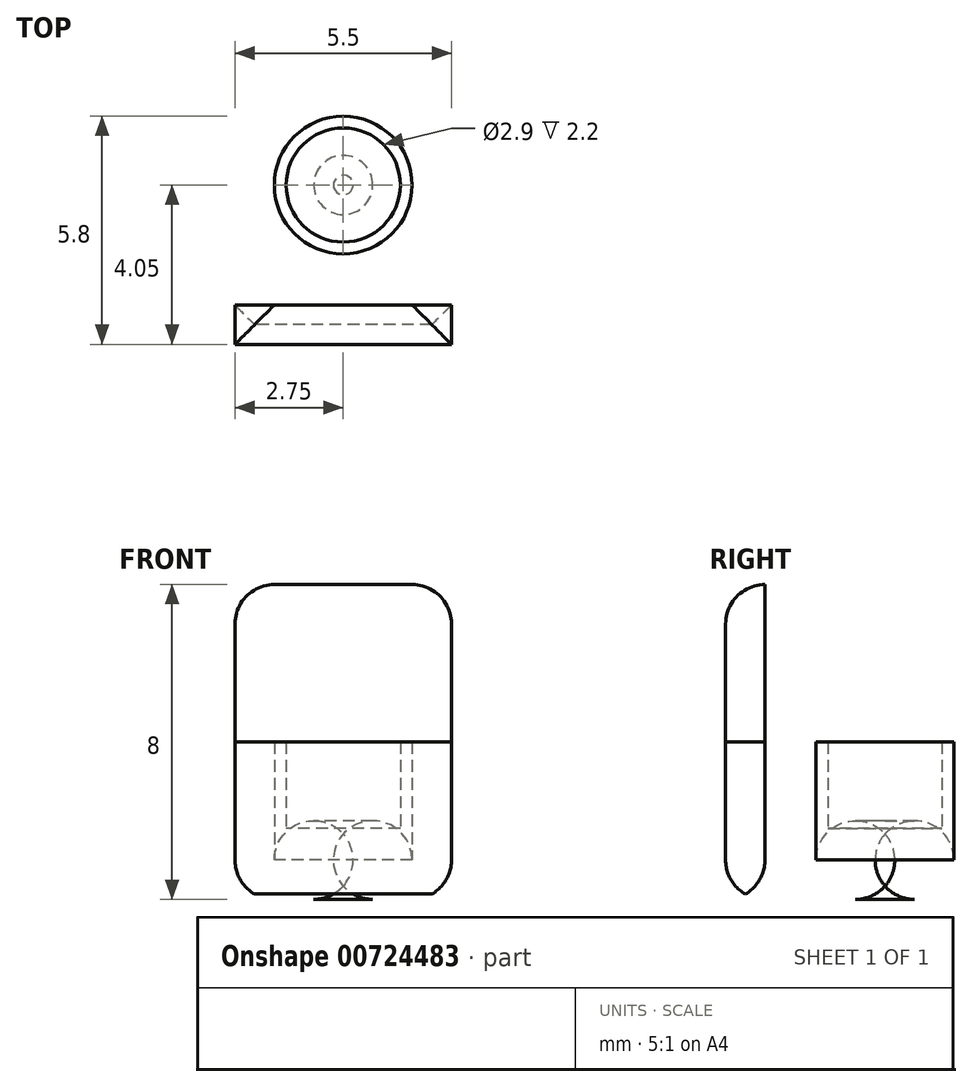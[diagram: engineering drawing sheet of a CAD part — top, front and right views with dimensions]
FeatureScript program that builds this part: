
annotation { "Feature Type Name" : "Feature", "Feature Type Description" : "" }
export const myFeature = defineFeature(function(context is Context, id is Id, definition is map)
    precondition{}
    {
        {
            var Q0;
            Q0=qCreatedBy(makeId("Top.planeOp"),FACE);
            var sketch = newSketch(context, id + "F0", { "sketchPlane" : qUnion([Q0])});
            skCircle(sketch, "E0", {"center": v(0, 4.05) * mm, "radius": 1.45 * mm});
            skLineSegment(sketch, "E1.bottom", {"start": v(0, 0) * mm, "end": v(2.75, 0) * mm});
            skLineSegment(sketch, "E1.top", {"start": v(0, 1) * mm, "end": v(2.75, 1) * mm});
            skLineSegment(sketch, "E1.left", {"start": v(0, 0) * mm, "end": v(0, 1) * mm});
            skLineSegment(sketch, "E1.right", {"start": v(2.75, 0) * mm, "end": v(2.75, 1) * mm});
            skCircle(sketch, "E2", {"center": v(0, 4.05) * mm, "radius": 1.75 * mm});
            skLineSegment(sketch, "E3", {"start": v(2.75, 1) * mm, "end": v(1.68, 4.56) * mm});
            skLineSegment(sketch, "E4", {"start": v(0, 1) * mm, "end": v(0, 2.3) * mm});
            skLineSegment(sketch, "E5.MirrorCS", {"start": v(-2.75, 1) * mm, "end": v(-1.68, 4.56) * mm});
            skLineSegment(sketch, "E6.MirrorCS", {"start": v(-2.75, 0) * mm, "end": v(-2.75, 1) * mm});
            skLineSegment(sketch, "E7.MirrorCS", {"start": v(0, 0) * mm, "end": v(-2.75, 0) * mm});
            skLineSegment(sketch, "E8.MirrorCS", {"start": v(0, 1) * mm, "end": v(-2.75, 1) * mm});
            skSolve(sketch);
        }
        {
            var Q0;
            Q0=makeQuery(id+"F0.imprint","IMPRINT",FACE,{"disambiguationData":[TD([[makeQuery(id+"F0.imprint","IMPRINT",EDGE,{"derivedFrom":sQuery(id+"F0.wireOp",EDGE,"E1.bottom")}),1.0]])]});
            var Q1;
            Q1=makeQuery(id+"F0.imprint","IMPRINT",FACE,{"disambiguationData":[TD([[makeQuery(id+"F0.imprint","IMPRINT",EDGE,{"derivedFrom":sQuery(id+"F0.wireOp",EDGE,"E1.left")}),1.0]])]});
            var Q2;
            Q2=makeQuery(id+"F0.imprint","IMPRINT",FACE,{"disambiguationData":[TD([[makeQuery(id+"F0.imprint","IMPRINT",EDGE,{"derivedFrom":sQuery(id+"F0.wireOp",EDGE,"E1.top")}),1.0]])]});
            var Q3;
            {var subQ0=sQuery(id+"F0.wireOp",EDGE,"E4");Q3=makeQuery(id+"F0.imprint","IMPRINT",FACE,{"disambiguationData":[TD([[makeQuery(id+"F0.imprint","IMPRINT",EDGE,{"derivedFrom":subQ0}),1.0]])]});}
            var Q4;
            Q4=makeQuery(id+"F0.imprint","IMPRINT",FACE,{"disambiguationData":[TD([[makeQuery(id+"F0.imprint","IMPRINT",EDGE,{"derivedFrom":sQuery(id+"F0.wireOp",EDGE,"E0")}),1.0]])]});
            var Q5;
            Q5=makeQuery(id+"F0.imprint","IMPRINT",FACE,{"disambiguationData":[TD([[makeQuery(id+"F0.imprint","IMPRINT",EDGE,{"derivedFrom":sQuery(id+"F0.wireOp",EDGE,"E0")}),-1.0]])]});
            extrude(context, id + "F1", {"entities" : qUnion([Q0, Q1, Q2, Q3, Q4, Q5]), "depth" : 1.8 * mm, "offsetDistance" : 25 * mm});
        }
        {
            var Q0;
            Q0=makeQuery(id+"F0.imprint","IMPRINT",FACE,{"disambiguationData":[TD([[makeQuery(id+"F0.imprint","IMPRINT",EDGE,{"derivedFrom":sQuery(id+"F0.wireOp",EDGE,"E0")}),-1.0]])]});
            var Q1;
            Q1=makeQuery(id+"F0.imprint","IMPRINT",FACE,{"disambiguationData":[TD([[makeQuery(id+"F0.imprint","IMPRINT",EDGE,{"derivedFrom":sQuery(id+"F0.wireOp",EDGE,"E1.left")}),1.0]])]});
            var Q2;
            Q2=makeQuery(id+"F0.imprint","IMPRINT",FACE,{"disambiguationData":[TD([[makeQuery(id+"F0.imprint","IMPRINT",EDGE,{"derivedFrom":sQuery(id+"F0.wireOp",EDGE,"E1.bottom")}),1.0]])]});
            extrude(context, id + "F2", {"entities" : qUnion([Q0, Q1, Q2]), "operationType" : NewBodyOperationType.ADD, "depth" : 4 * mm, "offsetDistance" : 25 * mm});
        }
        {
            var Q0;
            Q0=qCreatedBy(makeId("Top.planeOp"),FACE);
            cPlane(context, id + "F3", {"entities" : qUnion([Q0]), "cplaneType" : CPlaneType.OFFSET, "offset" : 4 * mm, "width" : 150 * mm, "height" : 150 * mm});
        }
        {
            var Q0;
            Q0=makeQuery(id+"F1.opExtrude","SWEPT_BODY",BODY,{"disambiguationData":[OSD([sQuery(id+"F0.wireOp",EDGE,"E1.bottom"),sQuery(id+"F0.wireOp",EDGE,"E1.right"),sQuery(id+"F0.wireOp",EDGE,"E3"),sQuery(id+"F0.wireOp",EDGE,"E2"),sQuery(id+"F0.wireOp",EDGE,"E5.MirrorCS"),sQuery(id+"F0.wireOp",EDGE,"E6.MirrorCS"),sQuery(id+"F0.wireOp",EDGE,"E7.MirrorCS")])]});
            var Q1;
            Q1=qCreatedBy(id+"F3.planeOp",FACE);
            mirror(context, id + "F4", {"operationType" : NewBodyOperationType.ADD, "entities" : qUnion([Q0]), "mirrorPlane" : qUnion([Q1])});
        }
        {
            var Q0;
            Q0=makeQuery(id+"F4.opPattern","COPY",EDGE,{"derivedFrom":makeQuery(id+"F1.opExtrude","CAP_EDGE",EDGE,{"disambiguationData":[OSD([sQuery(id+"F0.wireOp",EDGE,"E3")])],"isStart":true}),"instanceName":"1"});
            var Q1;
            Q1=makeQuery(id+"F4.opPattern","COPY",EDGE,{"derivedFrom":makeQuery(id+"F1.opExtrude","CAP_EDGE",EDGE,{"disambiguationData":[OSD([sQuery(id+"F0.wireOp",EDGE,"E2")])],"isStart":true}),"instanceName":"1"});
            var Q2;
            Q2=makeQuery(id+"F4.opPattern","COPY",EDGE,{"derivedFrom":makeQuery(id+"F1.opExtrude","CAP_EDGE",EDGE,{"disambiguationData":[OSD([sQuery(id+"F0.wireOp",EDGE,"E5.MirrorCS")])],"isStart":true}),"instanceName":"1"});
            var Q3;
            Q3=makeQuery(id+"F4.opPattern","COPY",EDGE,{"derivedFrom":makeQuery(id+"F1.opExtrude","CAP_EDGE",EDGE,{"disambiguationData":[OSD([sQuery(id+"F0.wireOp",EDGE,"E6.MirrorCS")])],"isStart":true}),"instanceName":"1"});
            var Q4;
            Q4=makeQuery(id+"F4.opPattern","COPY",EDGE,{"derivedFrom":makeQuery(id+"F1.opExtrude","CAP_EDGE",EDGE,{"disambiguationData":[OSD([sQuery(id+"F0.wireOp",EDGE,"E1.bottom"),sQuery(id+"F0.wireOp",EDGE,"E7.MirrorCS")])],"isStart":true}),"instanceName":"1"});
            var Q5;
            Q5=makeQuery(id+"F4.opPattern","COPY",EDGE,{"derivedFrom":makeQuery(id+"F1.opExtrude","CAP_EDGE",EDGE,{"disambiguationData":[OSD([sQuery(id+"F0.wireOp",EDGE,"E1.right")])],"isStart":true}),"instanceName":"1"});
            var Q6;
            Q6=makeQuery(id+"F1.opExtrude","CAP_EDGE",EDGE,{"disambiguationData":[OSD([sQuery(id+"F0.wireOp",EDGE,"E3")])],"isStart":true});
            var Q7;
            Q7=makeQuery(id+"F1.opExtrude","CAP_FACE",FACE,{"disambiguationData":[OSD([sQuery(id+"F0.wireOp",EDGE,"E1.bottom"),sQuery(id+"F0.wireOp",EDGE,"E1.right"),sQuery(id+"F0.wireOp",EDGE,"E3"),sQuery(id+"F0.wireOp",EDGE,"E2"),sQuery(id+"F0.wireOp",EDGE,"E5.MirrorCS"),sQuery(id+"F0.wireOp",EDGE,"E6.MirrorCS"),sQuery(id+"F0.wireOp",EDGE,"E7.MirrorCS")])],"isStart":true});
            var Q8;
            Q8=makeQuery(id+"F1.opExtrude","CAP_EDGE",EDGE,{"disambiguationData":[OSD([sQuery(id+"F0.wireOp",EDGE,"E2")])],"isStart":true});
            var Q9;
            Q9=makeQuery(id+"F1.opExtrude","CAP_EDGE",EDGE,{"disambiguationData":[OSD([sQuery(id+"F0.wireOp",EDGE,"E5.MirrorCS")])],"isStart":true});
            var Q10;
            Q10=makeQuery(id+"F1.opExtrude","CAP_EDGE",EDGE,{"disambiguationData":[OSD([sQuery(id+"F0.wireOp",EDGE,"E6.MirrorCS")])],"isStart":true});
            fillet(context, id + "F5", {"entities" : qUnion([Q0, Q1, Q2, Q3, Q4, Q5, Q6, Q7, Q8, Q9, Q10]), "radius" : 1 * mm, "tangentPropagation" : true, "allowEdgeOverflow" : false});
        }
    });
